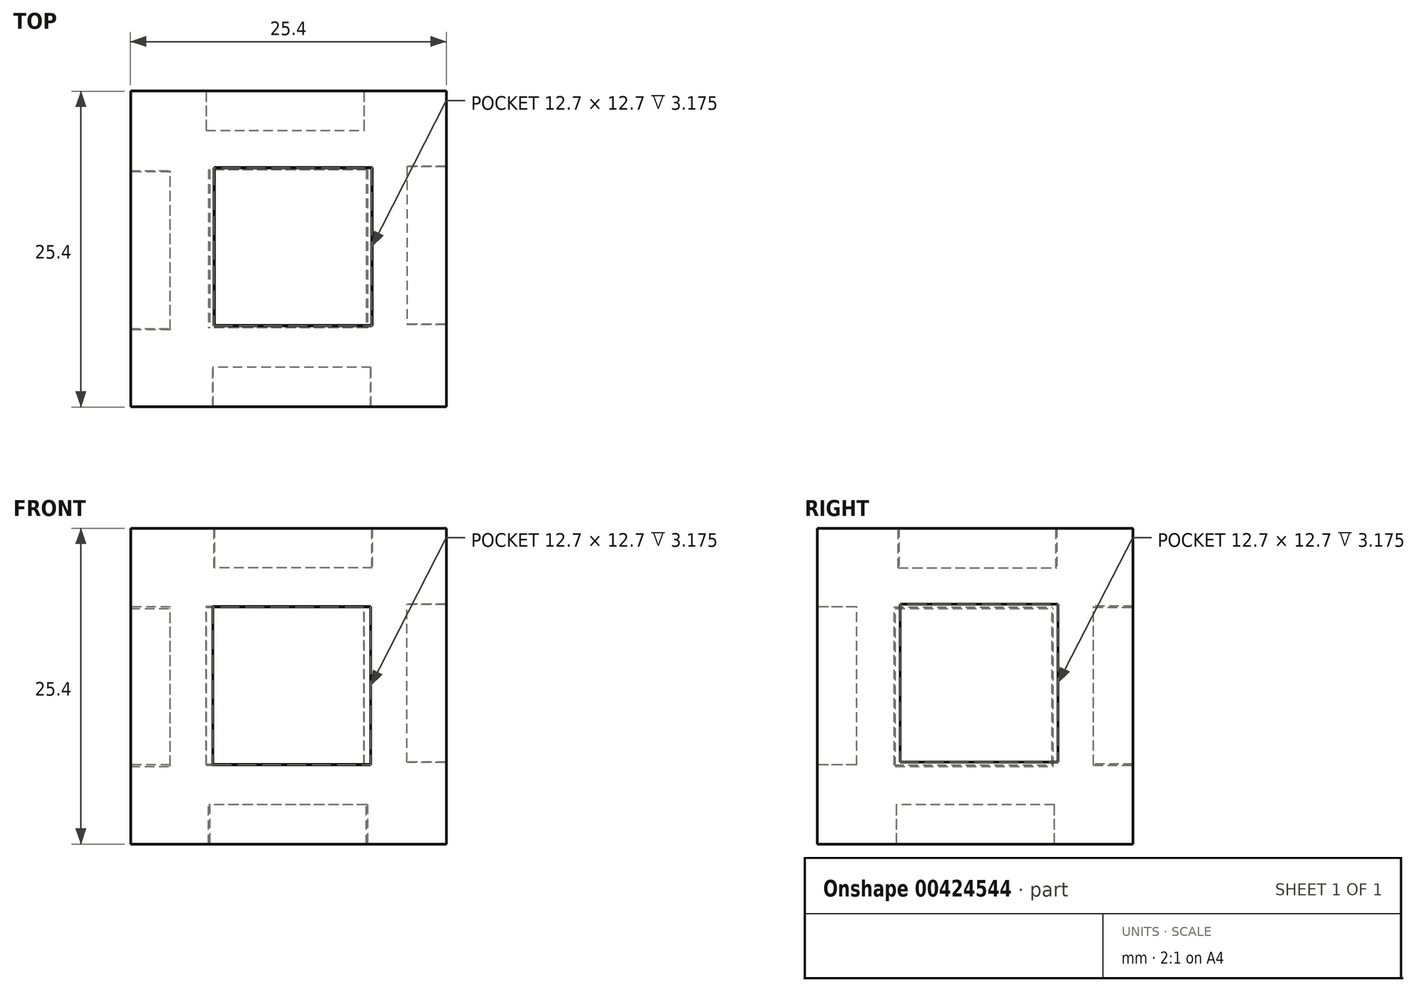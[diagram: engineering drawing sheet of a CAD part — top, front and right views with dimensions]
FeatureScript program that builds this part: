
annotation { "Feature Type Name" : "Feature", "Feature Type Description" : "" }
export const myFeature = defineFeature(function(context is Context, id is Id, definition is map)
    precondition{}
    {
        {
            var Q0;
            Q0=qCreatedBy(makeId("Top.planeOp"),FACE);
            var sketch = newSketch(context, id + "F0", { "sketchPlane" : qUnion([Q0])});
            skLineSegment(sketch, "E0.bottom", {"start": v(12.12, 0.42) * mm, "end": v(-13.28, 0.42) * mm});
            skLineSegment(sketch, "E0.top", {"start": v(12.12, 25.82) * mm, "end": v(-13.28, 25.82) * mm});
            skLineSegment(sketch, "E0.left", {"start": v(12.12, 0.42) * mm, "end": v(12.12, 25.82) * mm});
            skLineSegment(sketch, "E0.right", {"start": v(-13.28, 0.42) * mm, "end": v(-13.28, 25.82) * mm});
            skPoint(sketch, "E0.middle", {"position": v(-0.58, 13.12) * mm});
            skSolve(sketch);
        }
        {
            var Q0;
            Q0 = qSketchRegion(id + "F0", true);
            extrude(context, id + "F1", {"entities" : qUnion([Q0]), "depth" : 25.4 * mm});
        }
        {
            var Q0;
            Q0=makeQuery(id+"F1.opExtrude","CAP_FACE",FACE,{"disambiguationData":[OSD([sQuery(id+"F0.wireOp",EDGE,"E0.bottom"),sQuery(id+"F0.wireOp",EDGE,"E0.top"),sQuery(id+"F0.wireOp",EDGE,"E0.left"),sQuery(id+"F0.wireOp",EDGE,"E0.right")])],"isStart":false});
            var sketch = newSketch(context, id + "F2", { "sketchPlane" : qUnion([Q0])});
            skLineSegment(sketch, "E1.bottom", {"start": v(6.14, 6.93) * mm, "end": v(-6.56, 6.93) * mm});
            skLineSegment(sketch, "E1.top", {"start": v(6.14, 19.63) * mm, "end": v(-6.56, 19.63) * mm});
            skLineSegment(sketch, "E1.left", {"start": v(6.14, 6.93) * mm, "end": v(6.14, 19.63) * mm});
            skLineSegment(sketch, "E1.right", {"start": v(-6.56, 6.93) * mm, "end": v(-6.56, 19.63) * mm});
            skPoint(sketch, "E1.middle", {"position": v(-0.2, 13.28) * mm});
            skLineSegment(sketch, "E2.bottom", {"start": v(25.19, 67.38) * mm, "end": v(49.38, 67.38) * mm});
            skLineSegment(sketch, "E2.top", {"start": v(25.19, 54.07) * mm, "end": v(49.38, 54.07) * mm});
            skLineSegment(sketch, "E2.left", {"start": v(25.19, 67.38) * mm, "end": v(25.19, 54.07) * mm});
            skLineSegment(sketch, "E2.right", {"start": v(49.38, 67.38) * mm, "end": v(49.38, 54.07) * mm});
            skPoint(sketch, "E2.middle", {"position": v(37.28, 60.73) * mm});
            skSolve(sketch);
        }
        {
            var Q0;
            Q0=makeQuery(id+"F2.imprint","IMPRINT",FACE,{"disambiguationData":[TD([[makeQuery(id+"F2.imprint","IMPRINT",EDGE,{"derivedFrom":sQuery(id+"F2.wireOp",EDGE,"E1.bottom")}),-1.0]])]});
            extrude(context, id + "F3", {"entities" : qUnion([Q0]), "operationType" : NewBodyOperationType.REMOVE, "oppositeDirection" : true, "depth" : 3.17 * mm});
        }
        {
            var Q0;
            Q0=makeQuery(id+"F1.opExtrude","CAP_FACE",FACE,{"disambiguationData":[OSD([sQuery(id+"F0.wireOp",EDGE,"E0.bottom"),sQuery(id+"F0.wireOp",EDGE,"E0.top"),sQuery(id+"F0.wireOp",EDGE,"E0.left"),sQuery(id+"F0.wireOp",EDGE,"E0.right")])],"isStart":true});
            var sketch = newSketch(context, id + "F4", { "sketchPlane" : qUnion([Q0])});
            skLineSegment(sketch, "E3.bottom", {"start": v(5.77, -19.47) * mm, "end": v(-6.93, -19.47) * mm});
            skLineSegment(sketch, "E3.top", {"start": v(5.77, -6.77) * mm, "end": v(-6.93, -6.77) * mm});
            skLineSegment(sketch, "E3.left", {"start": v(5.77, -19.47) * mm, "end": v(5.77, -6.77) * mm});
            skLineSegment(sketch, "E3.right", {"start": v(-6.93, -19.47) * mm, "end": v(-6.93, -6.77) * mm});
            skPoint(sketch, "E3.middle", {"position": v(-0.58, -13.12) * mm});
            skPoint(sketch, "E3.middle.positionSnap0", {"position": v(-13.28, -13.12) * mm});
            skPoint(sketch, "E3.centerSnap0", {"position": v(-13.28, -13.12) * mm});
            skSolve(sketch);
        }
        {
            var Q0;
            Q0=makeQuery(id+"F4.imprint","IMPRINT",FACE,{"disambiguationData":[TD([[makeQuery(id+"F4.imprint","IMPRINT",EDGE,{"derivedFrom":sQuery(id+"F4.wireOp",EDGE,"E3.bottom")}),-1.0]])]});
            extrude(context, id + "F5", {"entities" : qUnion([Q0]), "operationType" : NewBodyOperationType.REMOVE, "oppositeDirection" : true, "depth" : 3.17 * mm});
        }
        {
            var Q0;
            Q0=makeQuery(id+"F1.opExtrude","SWEPT_FACE",FACE,{"disambiguationData":[OSD([sQuery(id+"F0.wireOp",EDGE,"E0.bottom")])]});
            var sketch = newSketch(context, id + "F6", { "sketchPlane" : qUnion([Q0])});
            skLineSegment(sketch, "E4.bottom", {"start": v(6.05, 6.36) * mm, "end": v(-6.65, 6.36) * mm});
            skLineSegment(sketch, "E4.top", {"start": v(6.05, 19.06) * mm, "end": v(-6.65, 19.06) * mm});
            skLineSegment(sketch, "E4.left", {"start": v(6.05, 6.36) * mm, "end": v(6.05, 19.06) * mm});
            skLineSegment(sketch, "E4.right", {"start": v(-6.65, 6.36) * mm, "end": v(-6.65, 19.06) * mm});
            skSolve(sketch);
        }
        {
            var Q0;
            Q0 = qSketchRegion(id + "F6", true);
            extrude(context, id + "F7", {"entities" : qUnion([Q0]), "operationType" : NewBodyOperationType.REMOVE, "oppositeDirection" : true, "depth" : 3.17 * mm});
        }
        {
            var Q0;
            Q0=makeQuery(id+"F1.opExtrude","SWEPT_FACE",FACE,{"disambiguationData":[OSD([sQuery(id+"F0.wireOp",EDGE,"E0.left")])]});
            var sketch = newSketch(context, id + "F8", { "sketchPlane" : qUnion([Q0])});
            skLineSegment(sketch, "E5.bottom", {"start": v(19.77, 6.6) * mm, "end": v(7.07, 6.6) * mm});
            skLineSegment(sketch, "E5.top", {"start": v(19.77, 19.3) * mm, "end": v(7.07, 19.3) * mm});
            skLineSegment(sketch, "E5.left", {"start": v(19.77, 6.6) * mm, "end": v(19.77, 19.3) * mm});
            skLineSegment(sketch, "E5.right", {"start": v(7.07, 6.6) * mm, "end": v(7.07, 19.3) * mm});
            skSolve(sketch);
        }
        {
            var Q0;
            Q0 = qSketchRegion(id + "F8", true);
            extrude(context, id + "F9", {"entities" : qUnion([Q0]), "operationType" : NewBodyOperationType.REMOVE, "oppositeDirection" : true, "depth" : 3.17 * mm});
        }
        {
            var Q0;
            Q0=makeQuery(id+"F1.opExtrude","SWEPT_FACE",FACE,{"disambiguationData":[OSD([sQuery(id+"F0.wireOp",EDGE,"E0.top")])]});
            var sketch = newSketch(context, id + "F10", { "sketchPlane" : qUnion([Q0])});
            skLineSegment(sketch, "E6.bottom", {"start": v(7.17, 6.35) * mm, "end": v(-5.53, 6.35) * mm});
            skLineSegment(sketch, "E6.top", {"start": v(7.17, 19.05) * mm, "end": v(-5.53, 19.05) * mm});
            skLineSegment(sketch, "E6.left", {"start": v(7.17, 6.35) * mm, "end": v(7.17, 19.05) * mm});
            skLineSegment(sketch, "E6.right", {"start": v(-5.53, 6.35) * mm, "end": v(-5.53, 19.05) * mm});
            skSolve(sketch);
        }
        {
            var Q0;
            Q0 = qSketchRegion(id + "F10", true);
            extrude(context, id + "F11", {"entities" : qUnion([Q0]), "operationType" : NewBodyOperationType.REMOVE, "oppositeDirection" : true, "depth" : 3.17 * mm});
        }
        {
            var Q0;
            Q0=makeQuery(id+"F1.opExtrude","SWEPT_FACE",FACE,{"disambiguationData":[OSD([sQuery(id+"F0.wireOp",EDGE,"E0.right")])]});
            var sketch = newSketch(context, id + "F12", { "sketchPlane" : qUnion([Q0])});
            skLineSegment(sketch, "E7.bottom", {"start": v(-6.61, 6.38) * mm, "end": v(-19.31, 6.38) * mm});
            skLineSegment(sketch, "E7.top", {"start": v(-6.61, 19.08) * mm, "end": v(-19.31, 19.08) * mm});
            skLineSegment(sketch, "E7.left", {"start": v(-6.61, 6.38) * mm, "end": v(-6.61, 19.08) * mm});
            skLineSegment(sketch, "E7.right", {"start": v(-19.31, 6.38) * mm, "end": v(-19.31, 19.08) * mm});
            skSolve(sketch);
        }
        {
            var Q0;
            Q0 = qSketchRegion(id + "F12", true);
            extrude(context, id + "F13", {"entities" : qUnion([Q0]), "operationType" : NewBodyOperationType.REMOVE, "oppositeDirection" : true, "depth" : 3.17 * mm});
        }
        {
            var Q0;
            Q0=makeQuery(id+"F3.boolean.opBoolean","COPY",FACE,{"derivedFrom":makeQuery(id+"F3.opExtrude","CAP_FACE",FACE,{"disambiguationData":[OSD([sQuery(id+"F2.wireOp",EDGE,"E1.bottom"),sQuery(id+"F2.wireOp",EDGE,"E1.top"),sQuery(id+"F2.wireOp",EDGE,"E1.left"),sQuery(id+"F2.wireOp",EDGE,"E1.right")])],"isStart":false})});
            var sketch = newSketch(context, id + "F14", { "sketchPlane" : qUnion([Q0])});
            skLineSegment(sketch, "E8.bottom", {"start": v(6.18, 6.98) * mm, "end": v(-6.52, 6.98) * mm});
            skLineSegment(sketch, "E8.top", {"start": v(6.18, 19.68) * mm, "end": v(-6.52, 19.68) * mm});
            skLineSegment(sketch, "E8.left", {"start": v(6.18, 6.98) * mm, "end": v(6.18, 19.68) * mm});
            skLineSegment(sketch, "E8.right", {"start": v(-6.52, 6.98) * mm, "end": v(-6.52, 19.68) * mm});
            skSolve(sketch);
        }
        {
            var Q0;
            Q0 = qSketchRegion(id + "F14", true);
            extrude(context, id + "F15", {"entities" : qUnion([Q0]), "depth" : 3.17 * mm});
        }
        {
            var Q0;
            Q0=makeQuery(id+"F7.boolean.opBoolean","COPY",FACE,{"derivedFrom":makeQuery(id+"F7.opExtrude","CAP_FACE",FACE,{"disambiguationData":[OSD([sQuery(id+"F6.wireOp",EDGE,"E4.bottom"),sQuery(id+"F6.wireOp",EDGE,"E4.top"),sQuery(id+"F6.wireOp",EDGE,"E4.left"),sQuery(id+"F6.wireOp",EDGE,"E4.right")])],"isStart":false})});
            var sketch = newSketch(context, id + "F16", { "sketchPlane" : qUnion([Q0])});
            skLineSegment(sketch, "E9.bottom", {"start": v(6.05, 6.4) * mm, "end": v(-6.65, 6.4) * mm});
            skLineSegment(sketch, "E9.top", {"start": v(6.05, 19.1) * mm, "end": v(-6.65, 19.1) * mm});
            skLineSegment(sketch, "E9.left", {"start": v(6.05, 6.4) * mm, "end": v(6.05, 19.1) * mm});
            skLineSegment(sketch, "E9.right", {"start": v(-6.65, 6.4) * mm, "end": v(-6.65, 19.1) * mm});
            skSolve(sketch);
        }
        {
            var Q0;
            Q0 = qSketchRegion(id + "F16", true);
            extrude(context, id + "F17", {"entities" : qUnion([Q0]), "depth" : 3.17 * mm});
        }
        {
            var Q0;
            Q0=makeQuery(id+"F9.boolean.opBoolean","COPY",FACE,{"derivedFrom":makeQuery(id+"F9.opExtrude","CAP_FACE",FACE,{"disambiguationData":[OSD([sQuery(id+"F8.wireOp",EDGE,"E5.bottom"),sQuery(id+"F8.wireOp",EDGE,"E5.top"),sQuery(id+"F8.wireOp",EDGE,"E5.left"),sQuery(id+"F8.wireOp",EDGE,"E5.right")])],"isStart":false})});
            var sketch = newSketch(context, id + "F18", { "sketchPlane" : qUnion([Q0])});
            skLineSegment(sketch, "E10.bottom", {"start": v(19.78, 6.6) * mm, "end": v(7.08, 6.6) * mm});
            skLineSegment(sketch, "E10.top", {"start": v(19.78, 19.3) * mm, "end": v(7.08, 19.3) * mm});
            skLineSegment(sketch, "E10.left", {"start": v(19.78, 6.6) * mm, "end": v(19.78, 19.3) * mm});
            skLineSegment(sketch, "E10.right", {"start": v(7.08, 6.6) * mm, "end": v(7.08, 19.3) * mm});
            skSolve(sketch);
        }
        {
            var Q0;
            Q0 = qSketchRegion(id + "F18", true);
            extrude(context, id + "F19", {"entities" : qUnion([Q0]), "depth" : 3.17 * mm});
        }
        {
            var Q0;
            Q0=makeQuery(id+"F11.boolean.opBoolean","COPY",FACE,{"derivedFrom":makeQuery(id+"F11.opExtrude","CAP_FACE",FACE,{"disambiguationData":[OSD([sQuery(id+"F10.wireOp",EDGE,"E6.bottom"),sQuery(id+"F10.wireOp",EDGE,"E6.top"),sQuery(id+"F10.wireOp",EDGE,"E6.left"),sQuery(id+"F10.wireOp",EDGE,"E6.right")])],"isStart":false})});
            var sketch = newSketch(context, id + "F20", { "sketchPlane" : qUnion([Q0])});
            skLineSegment(sketch, "E11.bottom", {"start": v(7.2, 6.45) * mm, "end": v(-5.5, 6.45) * mm});
            skLineSegment(sketch, "E11.top", {"start": v(7.2, 19.15) * mm, "end": v(-5.5, 19.15) * mm});
            skLineSegment(sketch, "E11.left", {"start": v(7.2, 6.45) * mm, "end": v(7.2, 19.15) * mm});
            skLineSegment(sketch, "E11.right", {"start": v(-5.5, 6.45) * mm, "end": v(-5.5, 19.15) * mm});
            skSolve(sketch);
        }
        {
            var Q0;
            Q0 = qSketchRegion(id + "F20", true);
            extrude(context, id + "F21", {"entities" : qUnion([Q0]), "depth" : 3.17 * mm});
        }
        {
            var Q0;
            Q0=makeQuery(id+"F13.boolean.opBoolean","COPY",FACE,{"derivedFrom":makeQuery(id+"F13.opExtrude","CAP_FACE",FACE,{"disambiguationData":[OSD([sQuery(id+"F12.wireOp",EDGE,"E7.bottom"),sQuery(id+"F12.wireOp",EDGE,"E7.top"),sQuery(id+"F12.wireOp",EDGE,"E7.left"),sQuery(id+"F12.wireOp",EDGE,"E7.right")])],"isStart":false})});
            var sketch = newSketch(context, id + "F22", { "sketchPlane" : qUnion([Q0])});
            skLineSegment(sketch, "E12.bottom", {"start": v(-6.72, 6.26) * mm, "end": v(-19.42, 6.26) * mm});
            skLineSegment(sketch, "E12.top", {"start": v(-6.72, 18.96) * mm, "end": v(-19.42, 18.96) * mm});
            skLineSegment(sketch, "E12.left", {"start": v(-6.72, 6.26) * mm, "end": v(-6.72, 18.96) * mm});
            skLineSegment(sketch, "E12.right", {"start": v(-19.42, 6.26) * mm, "end": v(-19.42, 18.96) * mm});
            skSolve(sketch);
        }
        {
            var Q0;
            Q0 = qSketchRegion(id + "F22", true);
            extrude(context, id + "F23", {"entities" : qUnion([Q0]), "depth" : 3.17 * mm});
        }
        {
            var Q0;
            Q0=makeQuery(id+"F5.boolean.opBoolean","COPY",FACE,{"derivedFrom":makeQuery(id+"F5.opExtrude","CAP_FACE",FACE,{"disambiguationData":[OSD([sQuery(id+"F4.wireOp",EDGE,"E3.bottom"),sQuery(id+"F4.wireOp",EDGE,"E3.top"),sQuery(id+"F4.wireOp",EDGE,"E3.left"),sQuery(id+"F4.wireOp",EDGE,"E3.right")])],"isStart":false})});
            var sketch = newSketch(context, id + "F24", { "sketchPlane" : qUnion([Q0])});
            skLineSegment(sketch, "E13.bottom", {"start": v(5.68, -19.5) * mm, "end": v(-7.02, -19.5) * mm});
            skLineSegment(sketch, "E13.top", {"start": v(5.68, -6.8) * mm, "end": v(-7.02, -6.8) * mm});
            skLineSegment(sketch, "E13.left", {"start": v(5.68, -19.5) * mm, "end": v(5.68, -6.8) * mm});
            skLineSegment(sketch, "E13.right", {"start": v(-7.02, -19.5) * mm, "end": v(-7.02, -6.8) * mm});
            skSolve(sketch);
        }
        {
            var Q0;
            Q0 = qSketchRegion(id + "F24", true);
            extrude(context, id + "F25", {"entities" : qUnion([Q0]), "depth" : 3.17 * mm});
        }
    });
